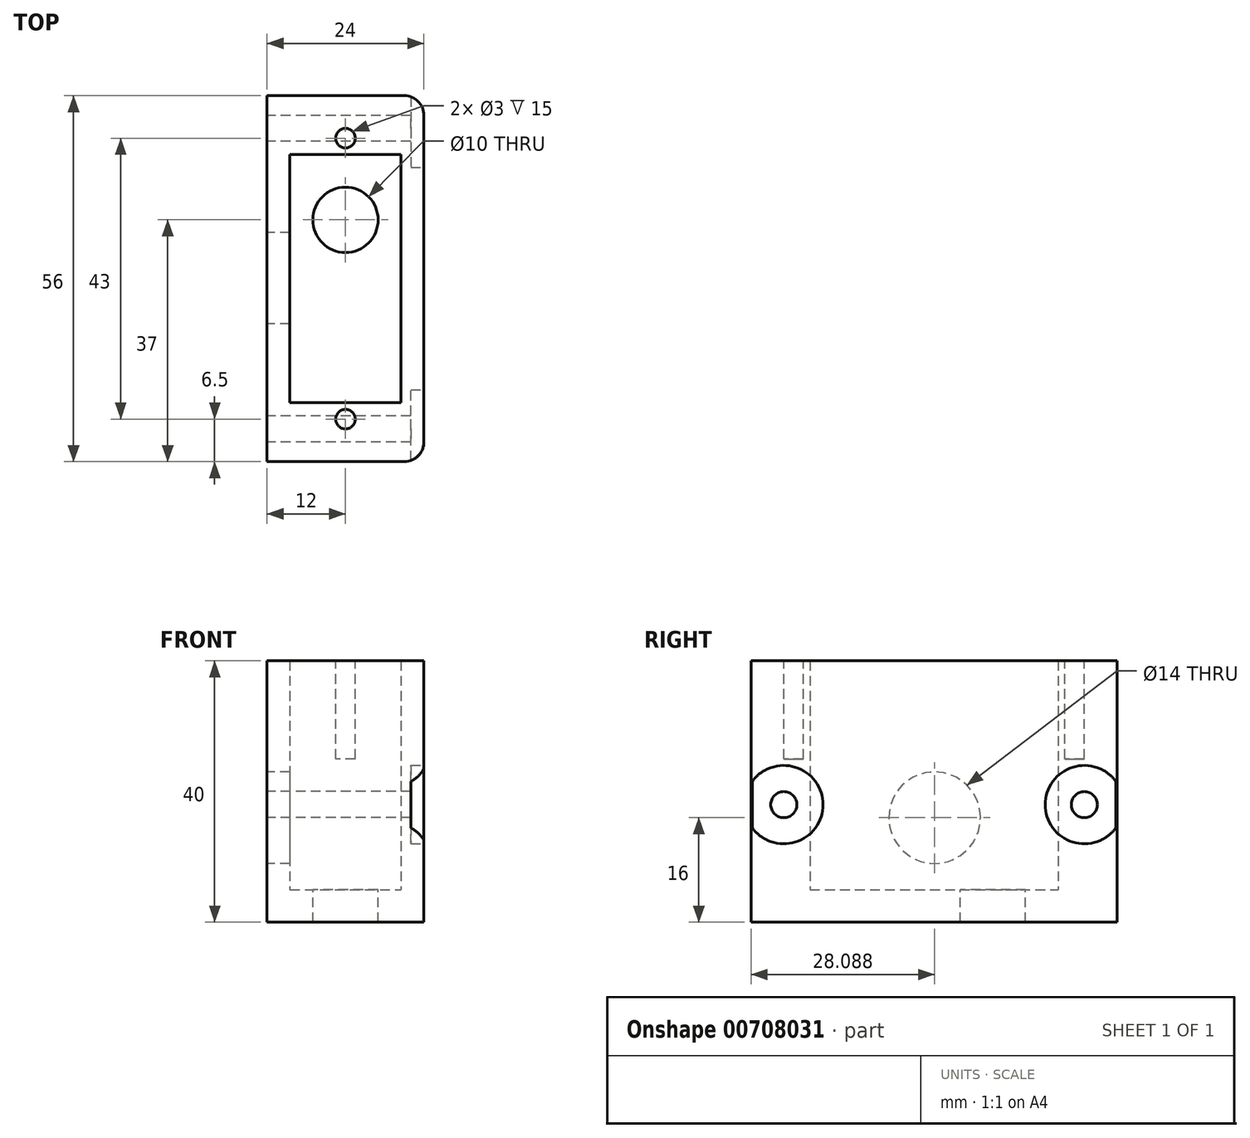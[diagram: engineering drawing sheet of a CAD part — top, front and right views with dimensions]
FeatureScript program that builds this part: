
annotation { "Feature Type Name" : "Feature", "Feature Type Description" : "" }
export const myFeature = defineFeature(function(context is Context, id is Id, definition is map)
    precondition{}
    {
        {
            var Q0;
            Q0=qCreatedBy(makeId("Top.planeOp"),FACE);
            var sketch = newSketch(context, id + "F0", { "sketchPlane" : qUnion([Q0])});
            skLineSegment(sketch, "E0.bottom", {"start": v(0, 0) * mm, "end": v(24, 0) * mm});
            skLineSegment(sketch, "E0.top", {"start": v(0, 56) * mm, "end": v(24, 56) * mm});
            skLineSegment(sketch, "E0.left", {"start": v(0, 0) * mm, "end": v(0, 56) * mm});
            skLineSegment(sketch, "E0.right", {"start": v(24, 0) * mm, "end": v(24, 56) * mm});
            skLineSegment(sketch, "E1.bottom", {"start": v(3.5, 9) * mm, "end": v(20.5, 9) * mm});
            skLineSegment(sketch, "E1.top", {"start": v(3.5, 47) * mm, "end": v(20.5, 47) * mm});
            skLineSegment(sketch, "E1.left", {"start": v(3.5, 9) * mm, "end": v(3.5, 47) * mm});
            skLineSegment(sketch, "E1.right", {"start": v(20.5, 9) * mm, "end": v(20.5, 47) * mm});
            skSolve(sketch);
        }
        {
            var Q0;
            Q0 = qSketchRegion(id + "F0", true);
            extrude(context, id + "F1", {"entities" : qUnion([Q0]), "depth" : 35 * mm, "offsetDistance" : 25 * mm});
        }
        {
            var Q0;
            Q0=makeQuery(id+"F1.opExtrude","CAP_FACE",FACE,{"disambiguationData":[OSD([sQuery(id+"F0.wireOp",EDGE,"E0.bottom"),sQuery(id+"F0.wireOp",EDGE,"E0.top"),sQuery(id+"F0.wireOp",EDGE,"E0.left"),sQuery(id+"F0.wireOp",EDGE,"E0.right"),sQuery(id+"F0.wireOp",EDGE,"E1.bottom"),sQuery(id+"F0.wireOp",EDGE,"E1.top"),sQuery(id+"F0.wireOp",EDGE,"E1.left"),sQuery(id+"F0.wireOp",EDGE,"E1.right")])],"isStart":false});
            var sketch = newSketch(context, id + "F2", { "sketchPlane" : qUnion([Q0])});
            skCircle(sketch, "E2", {"center": v(12, 49.5) * mm, "radius": 1.5 * mm});
            skPoint(sketch, "E2.centerSnap0", {"position": v(12, 47) * mm});
            skCircle(sketch, "E3", {"center": v(12, 6.5) * mm, "radius": 1.5 * mm});
            skPoint(sketch, "E3.centerSnap0", {"position": v(12, 9) * mm});
            skSolve(sketch);
        }
        {
            var Q0;
            Q0 = qSketchRegion(id + "F2", true);
            extrude(context, id + "F3", {"entities" : qUnion([Q0]), "operationType" : NewBodyOperationType.REMOVE, "oppositeDirection" : true, "depth" : 15 * mm, "offsetDistance" : 25 * mm});
        }
        {
            var Q0;
            Q0=makeQuery(id+"F1.opExtrude","SWEPT_EDGE",EDGE,{"disambiguationData":[OSD([sQuery(id+"F0.wireOp",EDGE,"E0.bottom"),sQuery(id+"F0.wireOp",EDGE,"E0.right")])]});
            var Q1;
            Q1=makeQuery(id+"F1.opExtrude","SWEPT_EDGE",EDGE,{"disambiguationData":[OSD([sQuery(id+"F0.wireOp",EDGE,"E0.top"),sQuery(id+"F0.wireOp",EDGE,"E0.right")])]});
            fillet(context, id + "F4", {"entities" : qUnion([Q0, Q1]), "radius" : 3 * mm, "tangentPropagation" : true, "allowEdgeOverflow" : false});
        }
        {
            var Q0;
            Q0=makeQuery(id+"F1.opExtrude","CAP_FACE",FACE,{"disambiguationData":[OSD([sQuery(id+"F0.wireOp",EDGE,"E0.bottom"),sQuery(id+"F0.wireOp",EDGE,"E0.top"),sQuery(id+"F0.wireOp",EDGE,"E0.left"),sQuery(id+"F0.wireOp",EDGE,"E0.right"),sQuery(id+"F0.wireOp",EDGE,"E1.bottom"),sQuery(id+"F0.wireOp",EDGE,"E1.top"),sQuery(id+"F0.wireOp",EDGE,"E1.left"),sQuery(id+"F0.wireOp",EDGE,"E1.right")])],"isStart":true});
            var sketch = newSketch(context, id + "F5", { "sketchPlane" : qUnion([Q0])});
            skLineSegment(sketch, "E4.0", {"start": v(0, 0) * mm, "end": v(21, 0) * mm});
            skArc(sketch, "E5.0", {"start": v(24, -3) * mm, "mid": v(23.12, -0.88) * mm, "end": v(21, 0) * mm});
            skLineSegment(sketch, "E6.0", {"start": v(24, -3) * mm, "end": v(24, -53) * mm});
            skArc(sketch, "E7.0", {"start": v(21, -56) * mm, "mid": v(23.12, -55.12) * mm, "end": v(24, -53) * mm});
            skLineSegment(sketch, "E8.0", {"start": v(0, -56) * mm, "end": v(21, -56) * mm});
            skLineSegment(sketch, "E9.0", {"start": v(0, 0) * mm, "end": v(0, -56) * mm});
            skSolve(sketch);
        }
        {
            var Q0;
            Q0 = qSketchRegion(id + "F5", true);
            extrude(context, id + "F6", {"entities" : qUnion([Q0]), "operationType" : NewBodyOperationType.ADD, "depth" : 5 * mm, "offsetDistance" : 25 * mm});
        }
        {
            var Q0;
            Q0=makeQuery(id+"F6.opExtrude","CAP_FACE",FACE,{"disambiguationData":[OSD([sQuery(id+"F5.wireOp",EDGE,"E4.0"),sQuery(id+"F5.wireOp",EDGE,"E5.0"),sQuery(id+"F5.wireOp",EDGE,"E6.0"),sQuery(id+"F5.wireOp",EDGE,"E7.0"),sQuery(id+"F5.wireOp",EDGE,"E8.0"),sQuery(id+"F5.wireOp",EDGE,"E9.0")])],"isStart":true});
            var sketch = newSketch(context, id + "F7", { "sketchPlane" : qUnion([Q0])});
            skCircle(sketch, "E10", {"center": v(12, 37) * mm, "radius": 5 * mm});
            skSolve(sketch);
        }
        {
            var Q0;
            Q0 = qSketchRegion(id + "F7", true);
            extrude(context, id + "F8", {"entities" : qUnion([Q0]), "operationType" : NewBodyOperationType.REMOVE, "oppositeDirection" : true, "depth" : 25 * mm, "offsetDistance" : 25 * mm});
        }
        {
            var Q0;
            Q0=makeQuery(id+"F6.boolean.opBoolean","MERGE",FACE,{"derivedFrom":[makeQuery(id+"F1.opExtrude","SWEPT_FACE",FACE,{"disambiguationData":[OSD([sQuery(id+"F0.wireOp",EDGE,"E0.left")])]}),makeQuery(id+"F6.opExtrude","SWEPT_FACE",FACE,{"disambiguationData":[OSD([sQuery(id+"F5.wireOp",EDGE,"E9.0")])]})]});
            var sketch = newSketch(context, id + "F9", { "sketchPlane" : qUnion([Q0])});
            skCircle(sketch, "E11", {"center": v(-51, 13) * mm, "radius": 2 * mm});
            skCircle(sketch, "E12", {"center": v(-5, 13) * mm, "radius": 2 * mm});
            skSolve(sketch);
        }
        {
            var Q0;
            Q0 = qSketchRegion(id + "F9", true);
            extrude(context, id + "F10", {"entities" : qUnion([Q0]), "operationType" : NewBodyOperationType.REMOVE, "oppositeDirection" : true, "depth" : 25 * mm, "offsetDistance" : 25 * mm});
        }
        {
            var Q0;
            Q0=makeQuery(id+"F6.boolean.opBoolean","MERGE",FACE,{"derivedFrom":[makeQuery(id+"F1.opExtrude","SWEPT_FACE",FACE,{"disambiguationData":[OSD([sQuery(id+"F0.wireOp",EDGE,"E0.right")])]}),makeQuery(id+"F6.opExtrude","SWEPT_FACE",FACE,{"disambiguationData":[OSD([sQuery(id+"F5.wireOp",EDGE,"E6.0")])]})]});
            var sketch = newSketch(context, id + "F11", { "sketchPlane" : qUnion([Q0])});
            skCircle(sketch, "E13", {"center": v(5, 13) * mm, "radius": 6 * mm});
            skCircle(sketch, "E14", {"center": v(51, 13) * mm, "radius": 6 * mm});
            skSolve(sketch);
        }
        {
            var Q0;
            Q0 = qSketchRegion(id + "F11", true);
            extrude(context, id + "F12", {"entities" : qUnion([Q0]), "operationType" : NewBodyOperationType.REMOVE, "oppositeDirection" : true, "depth" : 2 * mm, "offsetDistance" : 25 * mm});
        }
        {
            var Q0;
            Q0=makeQuery(id+"F6.boolean.opBoolean","MERGE",FACE,{"derivedFrom":[makeQuery(id+"F1.opExtrude","SWEPT_FACE",FACE,{"disambiguationData":[OSD([sQuery(id+"F0.wireOp",EDGE,"E0.left")])]}),makeQuery(id+"F6.opExtrude","SWEPT_FACE",FACE,{"disambiguationData":[OSD([sQuery(id+"F5.wireOp",EDGE,"E9.0")])]})]});
            var sketch = newSketch(context, id + "F13", { "sketchPlane" : qUnion([Q0])});
            skCircle(sketch, "E15", {"center": v(-28.09, 11) * mm, "radius": 7 * mm});
            skSolve(sketch);
        }
        {
            var Q0;
            Q0 = qSketchRegion(id + "F13", true);
            extrude(context, id + "F14", {"entities" : qUnion([Q0]), "operationType" : NewBodyOperationType.REMOVE, "oppositeDirection" : true, "depth" : 4 * mm, "offsetDistance" : 25 * mm});
        }
    });
